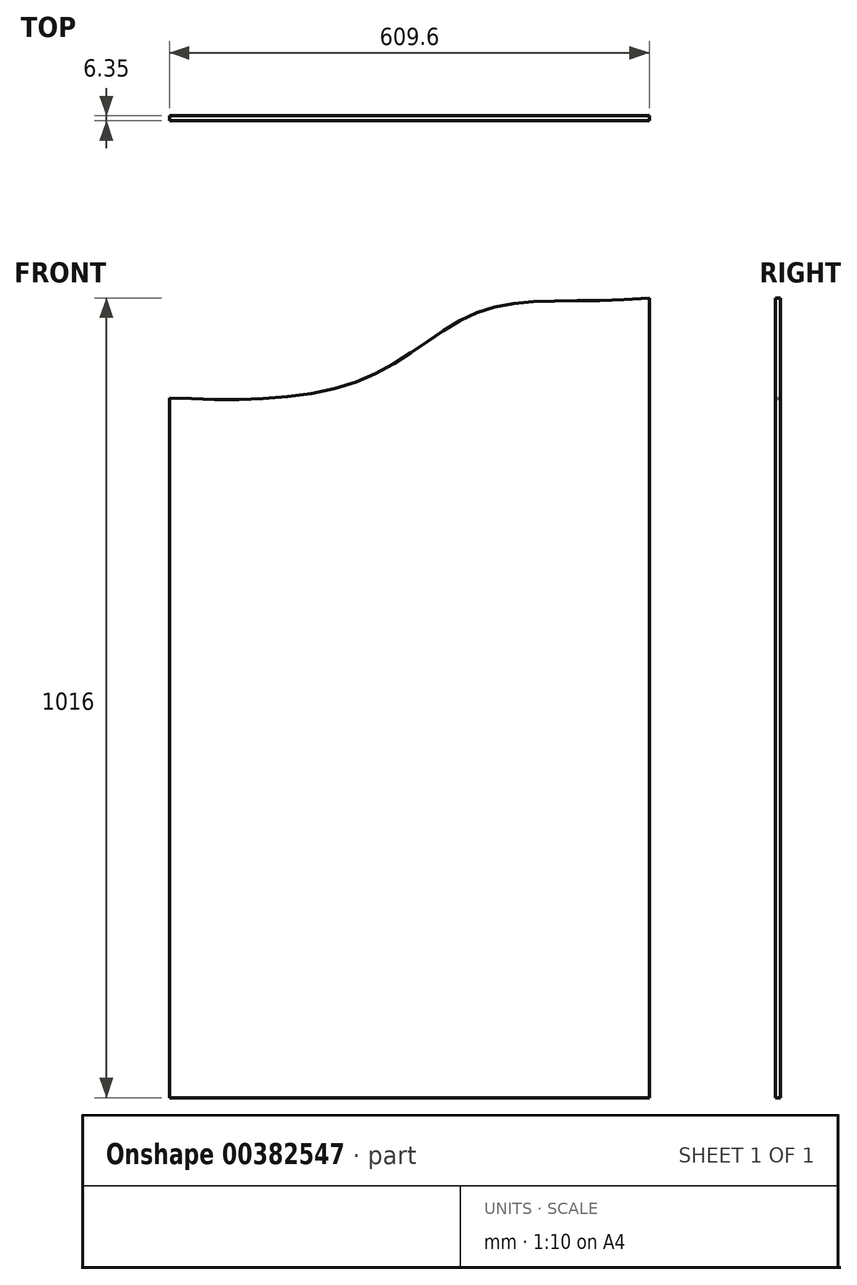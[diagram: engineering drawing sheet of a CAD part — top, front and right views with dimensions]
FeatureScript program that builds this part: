
annotation { "Feature Type Name" : "Feature", "Feature Type Description" : "" }
export const myFeature = defineFeature(function(context is Context, id is Id, definition is map)
    precondition{}
    {
        {
            var Q0;
            Q0=qCreatedBy(makeId("Front.planeOp"),FACE);
            var sketch = newSketch(context, id + "F0", { "sketchPlane" : qUnion([Q0])});
            skLineSegment(sketch, "E0.bottom", {"start": v(304.8, 609.6) * mm, "end": v(-304.8, 609.6) * mm});
            skLineSegment(sketch, "E0.top", {"start": v(304.8, -609.6) * mm, "end": v(-304.8, -609.6) * mm});
            skLineSegment(sketch, "E0.left", {"start": v(304.8, 609.6) * mm, "end": v(304.8, -609.6) * mm});
            skLineSegment(sketch, "E0.right", {"start": v(-304.8, 609.6) * mm, "end": v(-304.8, -609.6) * mm});
            skPoint(sketch, "E0.middle", {"position": v(0, 0) * mm});
            skSolve(sketch);
        }
        {
            var Q0;
            Q0=makeQuery(id+"F0.imprint","IMPRINT",FACE,{"disambiguationData":[TD([[makeQuery(id+"F0.imprint","IMPRINT",EDGE,{"derivedFrom":sQuery(id+"F0.wireOp",EDGE,"E0.bottom")}),1.0]])]});
            extrude(context, id + "F1", {"entities" : qUnion([Q0]), "depth" : 6.35 * mm});
        }
        {
            var Q0;
            Q0=makeQuery(id+"F1.opExtrude","CAP_FACE",FACE,{"disambiguationData":[OSD([sQuery(id+"F0.wireOp",EDGE,"E0.bottom"),sQuery(id+"F0.wireOp",EDGE,"E0.top"),sQuery(id+"F0.wireOp",EDGE,"E0.left"),sQuery(id+"F0.wireOp",EDGE,"E0.right")])],"isStart":false});
            var sketch = newSketch(context, id + "F2", { "sketchPlane" : qUnion([Q0])});
            skFitSpline(sketch, "E1", {"points": [v(304.8, 406.4) * mm, v(91.88, 389.92) * mm, v(-61, 301.9) * mm, v(-304.8, 279.4) * mm], "startDerivative": vector(-748.35, -76.8) * mm, "endDerivative": vector(-624.43, 28.63) * mm});
            skLineSegment(sketch, "E2", {"start": v(-304.8, 279.4) * mm, "end": v(-304.8, 609.6) * mm});
            skLineSegment(sketch, "E3", {"start": v(-304.8, 609.6) * mm, "end": v(304.8, 609.6) * mm});
            skLineSegment(sketch, "E4", {"start": v(304.8, 609.6) * mm, "end": v(304.8, 406.4) * mm});
            skSolve(sketch);
        }
        {
            var Q0;
            Q0=makeQuery(id+"F2.imprint","IMPRINT",FACE,{"disambiguationData":[TD([[makeQuery(id+"F2.imprint","IMPRINT",EDGE,{"derivedFrom":sQuery(id+"F2.wireOp",EDGE,"E1")}),-1.0]])]});
            extrude(context, id + "F3", {"entities" : qUnion([Q0]), "operationType" : NewBodyOperationType.REMOVE, "endBound" : BoundingType.THROUGH_ALL, "oppositeDirection" : true, "depth" : 25.4 * mm});
        }
    });
